# Revit family: Drain_Floor_Round-Zurn-Z415SH
name_source: partatom
category: Plumbing Fixtures
units: mm (PartAtom-declared; Revit-internal decimal feet)

## family parameters
Always vertical = Yes
Cut with Voids When Loaded = No
Maintain Annotation Orientation = No
OmniClass Number = 23.70.50.21.24.14
OmniClass Title = Deck Waste Water Drains
Part Type = Normal
Room Calculation Point = No
Round Connector Dimension = Use Radius
Shared = No
Work Plane-Based = No

## types (1)
- Drain_Floor_Round-Zurn-Z415SH
    Approx. Wt. Lbs. = 13.00 lb
    Assembly Code = D2030300
    Body Height (E) = 2.375 "
    CW Connection = No
    CWFU = 0
    Default Elevation = 30 "
    Description = BODY ASSEMBLY W/ “TYPE SH” STRAINER
    HW Connection = No
    HWFU = 0
    Manufacturer = Zurn Water, LLC
    Manufacurer Brand = Zurn
    Material Main = Iron - Zurn - Cast - Painted - Blue
    Model = ZN415SH
    Modified Date = 11/21/2025
    Pipe Size 'A' (Inner Diameter) = 2.067 "
    Pipe Size 'A' (Inner Radius) = 1.034 "
    Pipe Size 'A' (Nominal Diameter) = 2 "
    Pipe Size 'A' (Nominal Radius) = 1 "
    Pipe Size 'A' (Outer Diameter) = 2.375 "
    Pipe Size 'A' (Outer Radius) = 1.188 "
    Product Documentation Link = https://files.zurn.com
    Product Installation Sheet URL = https://files.zurn.com
    Product Page URL = https://www.zurn.com
    Product data url = https://www.bimobject.com
    Strainer (BxB) = 6 "
    Strainer Material = Bronze - Zurn - Polished Nickel
    Strainer Open Area = 12 in²
    Strainer Top Size 6"x6" Sq. = Yes
    Strainer Top Size 8"x8" Sq. = No
    Type Comments = ZN415SH 2 Inch IP Threaded Outlet
    URL = www.zurn.com
    Vent Connection = No
    WFU = 0
    Waste Connection = Yes
    z_Distance = 2.44 "

## geometry (parser evidence)
native form markers: Sweep x7
no freeform markers — native parametric forms only
